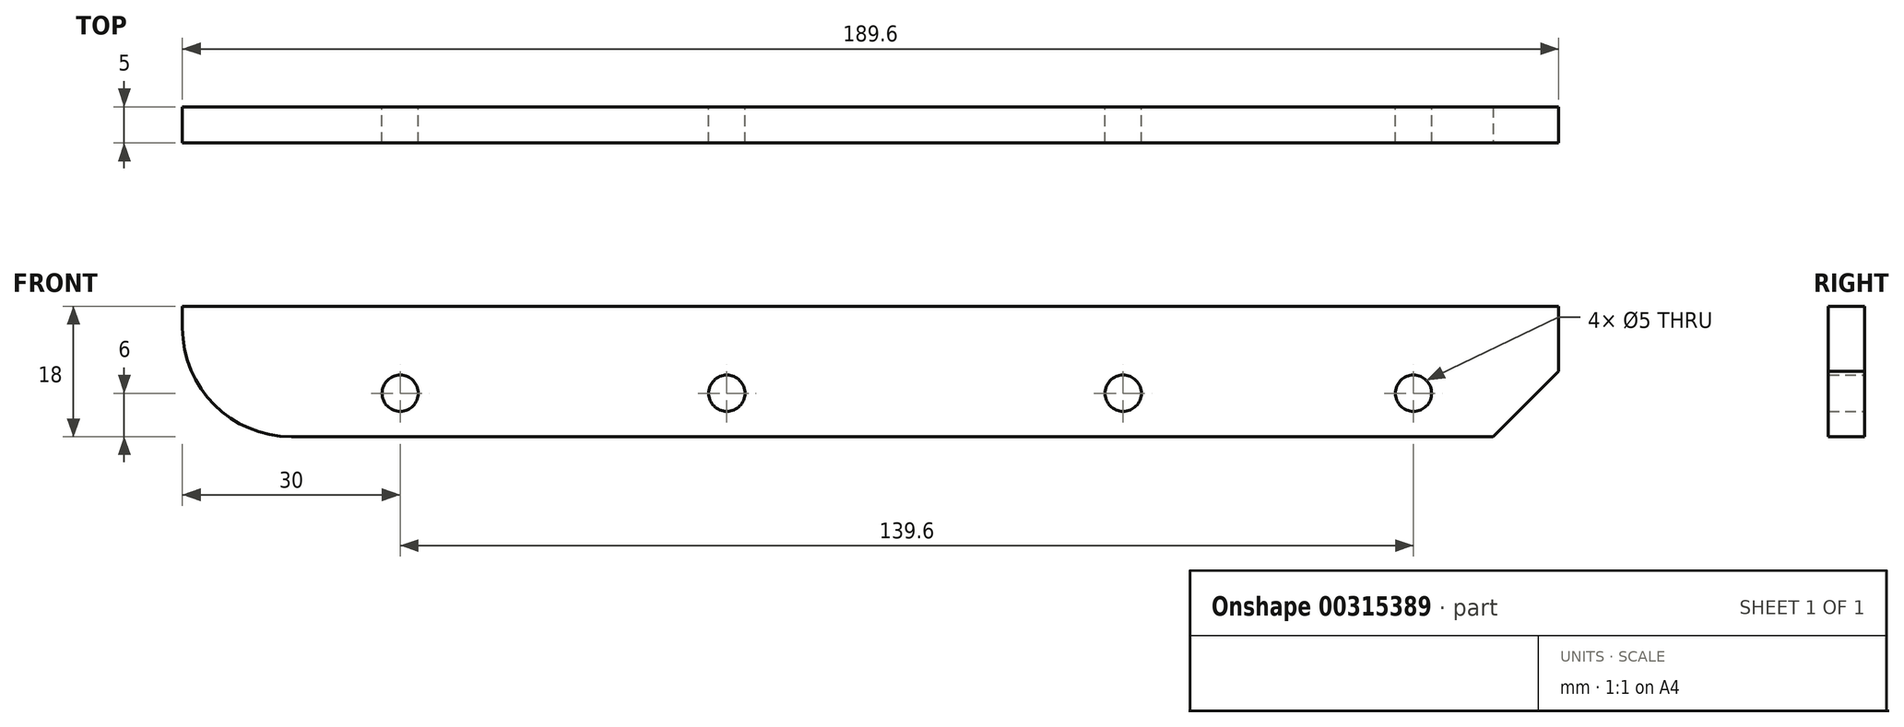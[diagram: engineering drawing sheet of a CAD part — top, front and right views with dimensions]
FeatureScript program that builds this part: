
annotation { "Feature Type Name" : "Feature", "Feature Type Description" : "" }
export const myFeature = defineFeature(function(context is Context, id is Id, definition is map)
    precondition{}
    {
        {
            var Q0;
            Q0=qCreatedBy(makeId("Front.planeOp"),FACE);
            var sketch = newSketch(context, id + "F0", { "sketchPlane" : qUnion([Q0])});
            skLineSegment(sketch, "E0.bottom", {"start": v(-94.8, 9) * mm, "end": v(94.8, 9) * mm});
            skLineSegment(sketch, "E0.top", {"start": v(-94.8, -9) * mm, "end": v(94.8, -9) * mm});
            skLineSegment(sketch, "E0.left", {"start": v(-94.8, 9) * mm, "end": v(-94.8, -9) * mm});
            skLineSegment(sketch, "E0.right", {"start": v(94.8, 9) * mm, "end": v(94.8, -9) * mm});
            skPoint(sketch, "E0.middle", {"position": v(0, 0) * mm});
            skLineSegment(sketch, "E1", {"start": v(-94.8, -3) * mm, "end": v(94.8, -3) * mm, "construction": true});
            skCircle(sketch, "E2", {"center": v(-64.8, -3) * mm, "radius": 2.5 * mm});
            skCircle(sketch, "E3", {"center": v(-19.8, -3) * mm, "radius": 2.5 * mm});
            skCircle(sketch, "E4", {"center": v(34.8, -3) * mm, "radius": 2.5 * mm});
            skCircle(sketch, "E5", {"center": v(74.8, -3) * mm, "radius": 2.5 * mm});
            skSolve(sketch);
        }
        {
            var Q0;
            Q0=makeQuery(id+"F0.imprint","IMPRINT",FACE,{"disambiguationData":[TD([[makeQuery(id+"F0.imprint","IMPRINT",EDGE,{"derivedFrom":sQuery(id+"F0.wireOp",EDGE,"E0.bottom")}),-1.0]])]});
            extrude(context, id + "F1", {"entities" : qUnion([Q0]), "depth" : 5 * mm});
        }
        {
            var Q0;
            Q0=makeQuery(id+"F1.opExtrude","CAP_FACE",FACE,{"disambiguationData":[OSD([sQuery(id+"F0.wireOp",EDGE,"E0.bottom"),sQuery(id+"F0.wireOp",EDGE,"E0.top"),sQuery(id+"F0.wireOp",EDGE,"E0.left"),sQuery(id+"F0.wireOp",EDGE,"E0.right"),sQuery(id+"F0.wireOp",EDGE,"E2"),sQuery(id+"F0.wireOp",EDGE,"E3"),sQuery(id+"F0.wireOp",EDGE,"E4"),sQuery(id+"F0.wireOp",EDGE,"E5")])],"isStart":false});
            var sketch = newSketch(context, id + "F2", { "sketchPlane" : qUnion([Q0])});
            skLineSegment(sketch, "E6.0.0", {"start": v(-94.8, 9) * mm, "end": v(-94.8, -9) * mm});
            skLineSegment(sketch, "E6.0.1", {"start": v(-94.8, -9) * mm, "end": v(94.8, -9) * mm});
            skLineSegment(sketch, "E6.0.2", {"start": v(94.8, -9) * mm, "end": v(94.8, 9) * mm});
            skLineSegment(sketch, "E6.0.3", {"start": v(94.8, 9) * mm, "end": v(-94.8, 9) * mm});
            skLineSegment(sketch, "E7", {"start": v(-94.8, 0) * mm, "end": v(-85.8, -9) * mm});
            skLineSegment(sketch, "E8", {"start": v(85.8, -9) * mm, "end": v(94.8, 0) * mm});
            skSolve(sketch);
        }
        {
            var Q0;
            {var subQ3=sQuery(id+"F2.wireOp",EDGE,"E8");Q0=makeQuery(id+"F2.imprint","IMPRINT",FACE,{"disambiguationData":[TD([[makeQuery(id+"F2.imprint","IMPRINT",EDGE,{"derivedFrom":subQ3}),-1.0]])]});}
            extrude(context, id + "F3", {"entities" : qUnion([Q0]), "operationType" : NewBodyOperationType.REMOVE, "oppositeDirection" : true, "depth" : 25 * mm});
        }
        {
            var Q0;
            Q0=makeQuery(id+"F1.opExtrude","SWEPT_EDGE",EDGE,{"disambiguationData":[OSD([sQuery(id+"F0.wireOp",EDGE,"E0.top"),sQuery(id+"F0.wireOp",EDGE,"E0.left")])]});
            fillet(context, id + "F4", {"entities" : qUnion([Q0]), "radius" : 15 * mm, "tangentPropagation" : true, "allowEdgeOverflow" : false});
        }
    });
